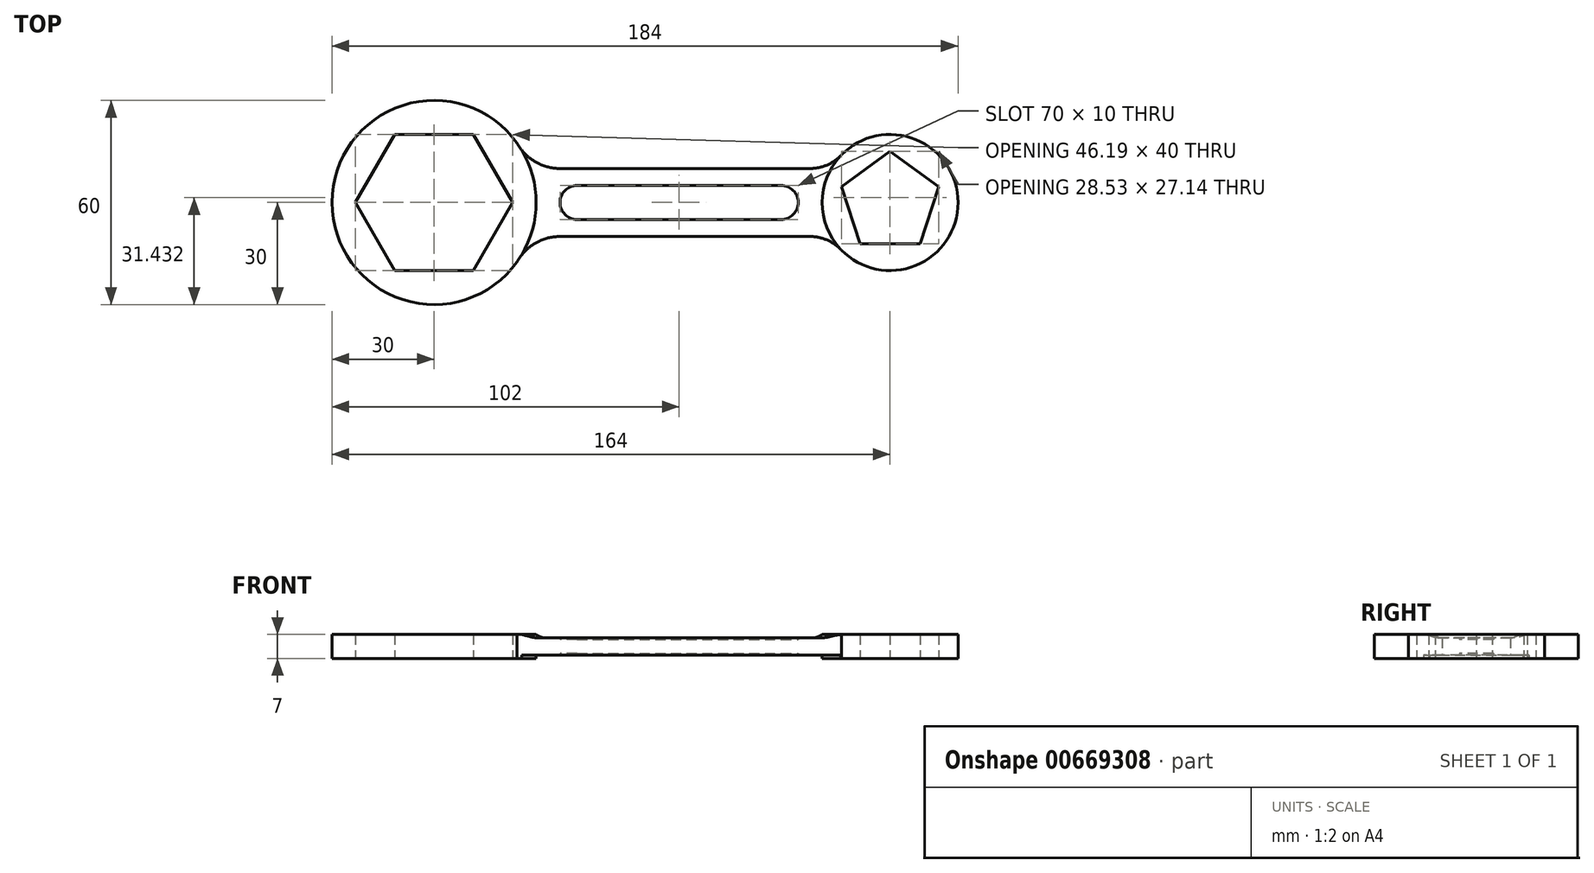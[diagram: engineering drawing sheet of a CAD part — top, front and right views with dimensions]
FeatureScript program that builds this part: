
annotation { "Feature Type Name" : "Feature", "Feature Type Description" : "" }
export const myFeature = defineFeature(function(context is Context, id is Id, definition is map)
    precondition{}
    {
        {
            var Q0;
            Q0=qCreatedBy(makeId("Top.planeOp"),FACE);
            var sketch = newSketch(context, id + "F0", { "sketchPlane" : qUnion([Q0])});
            skLineSegment(sketch, "E0.bottom", {"start": v(-30, -5) * mm, "end": v(30, -5) * mm});
            skLineSegment(sketch, "E0.top", {"start": v(-30, 5) * mm, "end": v(30, 5) * mm});
            skPoint(sketch, "E0.middle", {"position": v(0, 0) * mm});
            skArc(sketch, "E1", {"start": v(-30, 5) * mm, "mid": v(-35, 0) * mm, "end": v(-30, -5) * mm});
            skArc(sketch, "E2", {"start": v(30, -5) * mm, "mid": v(35, 0) * mm, "end": v(30, 5) * mm});
            skLineSegment(sketch, "E3", {"start": v(-35, 10) * mm, "end": v(38.5, 10) * mm});
            skPoint(sketch, "E3.startSnap0", {"position": v(-35, 0) * mm});
            skPoint(sketch, "E3.endSnap0", {"position": v(35, 0) * mm});
            skLineSegment(sketch, "E4", {"start": v(-35, -10) * mm, "end": v(38.5, -10) * mm});
            skCircle(sketch, "E5", {"center": v(-72, 0) * mm, "radius": 30 * mm});
            skCircle(sketch, "E6", {"center": v(62, 0) * mm, "radius": 20 * mm});
            skCircle(sketch, "E7.cCircle", {"center": v(-72, 0) * mm, "radius": 20 * mm, "construction": true});
            skLineSegment(sketch, "E7.0", {"start": v(-48.9, 0) * mm, "end": v(-60.45, -20) * mm});
            skLineSegment(sketch, "E7.1", {"start": v(-60.45, -20) * mm, "end": v(-83.55, -20) * mm});
            skLineSegment(sketch, "E7.2", {"start": v(-83.55, -20) * mm, "end": v(-95.1, 0) * mm});
            skLineSegment(sketch, "E7.3", {"start": v(-95.1, 0) * mm, "end": v(-83.55, 20) * mm});
            skLineSegment(sketch, "E7.4", {"start": v(-83.55, 20) * mm, "end": v(-60.45, 20) * mm});
            skLineSegment(sketch, "E7.5", {"start": v(-60.45, 20) * mm, "end": v(-48.9, 0) * mm});
            skPoint(sketch, "E7.0.midPoint", {"position": v(-54.68, -10) * mm});
            skCircle(sketch, "E8.cCircle", {"center": v(62, 0) * mm, "radius": 15 * mm, "construction": true});
            skLineSegment(sketch, "E8.0", {"start": v(53.18, -12.14) * mm, "end": v(47.73, 4.64) * mm});
            skLineSegment(sketch, "E8.1", {"start": v(47.73, 4.64) * mm, "end": v(62, 15) * mm});
            skLineSegment(sketch, "E8.2", {"start": v(62, 15) * mm, "end": v(76.27, 4.64) * mm});
            skLineSegment(sketch, "E8.3", {"start": v(76.27, 4.64) * mm, "end": v(70.82, -12.14) * mm});
            skLineSegment(sketch, "E8.4", {"start": v(70.82, -12.14) * mm, "end": v(53.18, -12.14) * mm});
            skArc(sketch, "E9", {"start": v(-47.63, 17.5) * mm, "mid": v(-42.35, 12.02) * mm, "end": v(-35, 10) * mm});
            skArc(sketch, "E10", {"start": v(-35, -10) * mm, "mid": v(-42.35, -12.02) * mm, "end": v(-47.63, -17.5) * mm});
            skArc(sketch, "E11", {"start": v(38.5, 10) * mm, "mid": v(43.52, 11.04) * mm, "end": v(47.72, 14) * mm});
            skArc(sketch, "E12", {"start": v(47.72, -14) * mm, "mid": v(43.52, -11.04) * mm, "end": v(38.5, -10) * mm});
            skLineSegment(sketch, "E13", {"start": v(38.5, -10) * mm, "end": v(38.5, 10) * mm});
            skSolve(sketch);
        }
        {
            var Q0;
            Q0=makeQuery(id+"F0.imprint","IMPRINT",FACE,{"disambiguationData":[TD([[makeQuery(id+"F0.imprint","IMPRINT",EDGE,{"derivedFrom":sQuery(id+"F0.wireOp",EDGE,"E0.bottom")}),-1.0]])]});
            var Q1;
            {var subQ5=sQuery(id+"F0.wireOp",EDGE,"E13");Q1=makeQuery(id+"F0.imprint","IMPRINT",FACE,{"disambiguationData":[TD([[makeQuery(id+"F0.imprint","IMPRINT",EDGE,{"derivedFrom":subQ5}),-1.0]])]});}
            extrude(context, id + "F1", {"entities" : qUnion([Q0, Q1]), "endBound" : BoundingType.SYMMETRIC, "depth" : 5 * mm, "offsetDistance" : 25 * mm});
        }
        {
            var Q0;
            Q0=makeQuery(id+"F0.imprint","IMPRINT",FACE,{"disambiguationData":[TD([[makeQuery(id+"F0.imprint","IMPRINT",EDGE,{"derivedFrom":sQuery(id+"F0.wireOp",EDGE,"E7.0")}),1.0]])]});
            var Q1;
            Q1=makeQuery(id+"F0.imprint","IMPRINT",FACE,{"disambiguationData":[TD([[makeQuery(id+"F0.imprint","IMPRINT",EDGE,{"derivedFrom":sQuery(id+"F0.wireOp",EDGE,"E8.0")}),1.0]])]});
            extrude(context, id + "F2", {"entities" : qUnion([Q0, Q1]), "operationType" : NewBodyOperationType.ADD, "endBound" : BoundingType.SYMMETRIC, "depth" : 7 * mm, "offsetDistance" : 25 * mm});
        }
        {
            var Q0;
            Q0=makeQuery(id+"F0.imprint","IMPRINT",FACE,{"disambiguationData":[TD([[makeQuery(id+"F0.imprint","IMPRINT",EDGE,{"derivedFrom":sQuery(id+"F0.wireOp",EDGE,"E0.bottom")}),1.0]])]});
            extrude(context, id + "F3", {"entities" : qUnion([Q0]), "operationType" : NewBodyOperationType.ADD, "endBound" : BoundingType.SYMMETRIC, "depth" : 4 * mm, "offsetDistance" : 25 * mm});
        }
        {
            var Q0;
            Q0=makeQuery(id+"F1.opExtrude","CAP_EDGE",EDGE,{"disambiguationData":[OSD([sQuery(id+"F0.wireOp",EDGE,"E5")])],"isStart":false});
            var Q1;
            Q1=makeQuery(id+"F1.opExtrude","CAP_EDGE",EDGE,{"disambiguationData":[OSD([sQuery(id+"F0.wireOp",EDGE,"E5")])],"isStart":true});
            var Q2;
            Q2=makeQuery(id+"F1.opExtrude","CAP_EDGE",EDGE,{"disambiguationData":[OSD([sQuery(id+"F0.wireOp",EDGE,"E6")])],"isStart":true});
            var Q3;
            Q3=makeQuery(id+"F1.opExtrude","CAP_EDGE",EDGE,{"disambiguationData":[OSD([sQuery(id+"F0.wireOp",EDGE,"E6")])],"isStart":false});
            fillet(context, id + "F4", {"entities" : qUnion([Q0, Q1, Q2, Q3]), "radius" : 5 * mm, "tangentPropagation" : true, "allowEdgeOverflow" : false});
        }
    });
